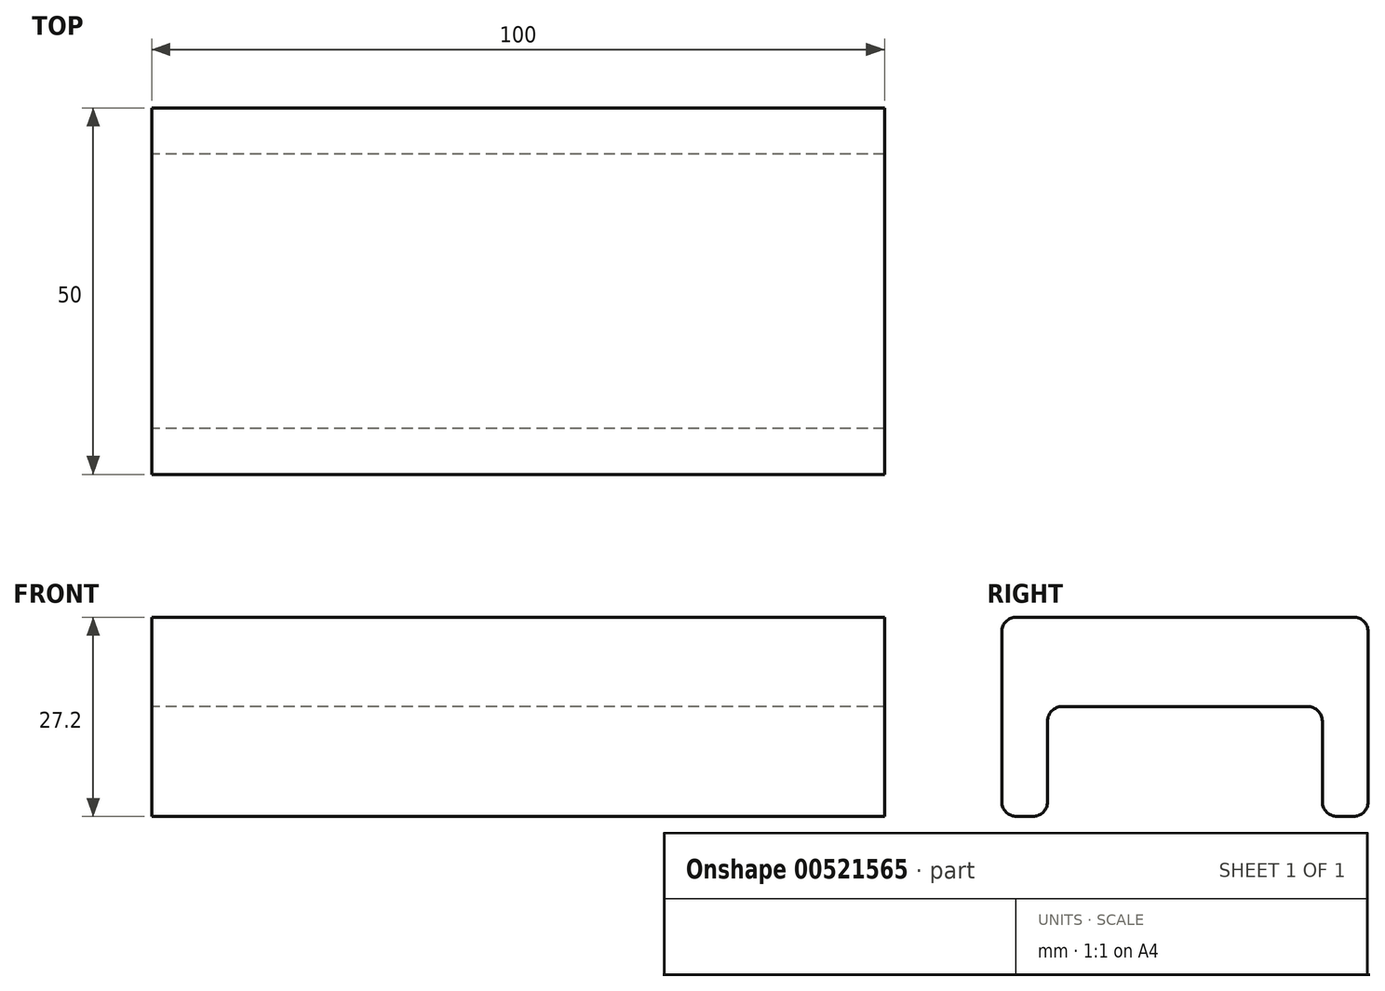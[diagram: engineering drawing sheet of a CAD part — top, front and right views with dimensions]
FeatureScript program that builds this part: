
annotation { "Feature Type Name" : "Feature", "Feature Type Description" : "" }
export const myFeature = defineFeature(function(context is Context, id is Id, definition is map)
    precondition{}
    {
        {
            var Q0;
            Q0=qCreatedBy(makeId("Right.planeOp"),FACE);
            var sketch = newSketch(context, id + "F0", { "sketchPlane" : qUnion([Q0])});
            skLineSegment(sketch, "E0.bottom", {"start": v(-23.91, 27.23) * mm, "end": v(22.09, 27.23) * mm});
            skLineSegment(sketch, "E0.top", {"start": v(-23.91, 0.03) * mm, "end": v(-21.66, 0.03) * mm});
            skLineSegment(sketch, "E0.left", {"start": v(-25.91, 25.23) * mm, "end": v(-25.91, 2.03) * mm});
            skLineSegment(sketch, "E0.right", {"start": v(24.09, 25.23) * mm, "end": v(24.09, 2.03) * mm});
            skLineSegment(sketch, "E1", {"start": v(-19.66, 2.03) * mm, "end": v(-19.66, 13.03) * mm});
            skLineSegment(sketch, "E2", {"start": v(-17.66, 15.03) * mm, "end": v(15.84, 15.03) * mm});
            skLineSegment(sketch, "E3", {"start": v(17.84, 13.03) * mm, "end": v(17.84, 2.03) * mm});
            skLineSegment(sketch, "E4.trimOffspring", {"start": v(19.84, 0.03) * mm, "end": v(22.09, 0.03) * mm});
            skPoint(sketch, "E5.visualSharp", {"position": v(17.84, 15.03) * mm});
            skArc(sketch, "E5.filletArc", {"start": v(17.84, 13.03) * mm, "mid": v(17.25, 14.44) * mm, "end": v(15.84, 15.03) * mm});
            skPoint(sketch, "E6.visualSharp", {"position": v(-19.66, 15.03) * mm});
            skArc(sketch, "E6.filletArc", {"start": v(-17.66, 15.03) * mm, "mid": v(-19.08, 14.44) * mm, "end": v(-19.66, 13.03) * mm});
            skPoint(sketch, "E7.visualSharp", {"position": v(24.09, 27.23) * mm});
            skArc(sketch, "E7.filletArc", {"start": v(24.09, 25.23) * mm, "mid": v(23.5, 26.64) * mm, "end": v(22.09, 27.23) * mm});
            skPoint(sketch, "E8.visualSharp", {"position": v(-25.91, 27.23) * mm});
            skArc(sketch, "E8.filletArc", {"start": v(-23.91, 27.23) * mm, "mid": v(-25.33, 26.64) * mm, "end": v(-25.91, 25.23) * mm});
            skPoint(sketch, "E9.visualSharp", {"position": v(-25.91, 0.03) * mm});
            skArc(sketch, "E9.filletArc", {"start": v(-25.91, 2.03) * mm, "mid": v(-25.33, 0.62) * mm, "end": v(-23.91, 0.03) * mm});
            skPoint(sketch, "E10.visualSharp", {"position": v(-19.66, 0.03) * mm});
            skArc(sketch, "E10.filletArc", {"start": v(-21.66, 0.03) * mm, "mid": v(-20.25, 0.62) * mm, "end": v(-19.66, 2.03) * mm});
            skPoint(sketch, "E11.visualSharp", {"position": v(17.84, 0.03) * mm});
            skArc(sketch, "E11.filletArc", {"start": v(17.84, 2.03) * mm, "mid": v(18.42, 0.62) * mm, "end": v(19.84, 0.03) * mm});
            skPoint(sketch, "E12.visualSharp", {"position": v(24.09, 0.03) * mm});
            skArc(sketch, "E12.filletArc", {"start": v(22.09, 0.03) * mm, "mid": v(23.5, 0.62) * mm, "end": v(24.09, 2.03) * mm});
            skSolve(sketch);
        }
        {
            var Q0;
            Q0 = qSketchRegion(id + "F0", true);
            extrude(context, id + "F1", {"entities" : qUnion([Q0]), "depth" : 100 * mm, "offsetDistance" : 25 * mm});
        }
    });
